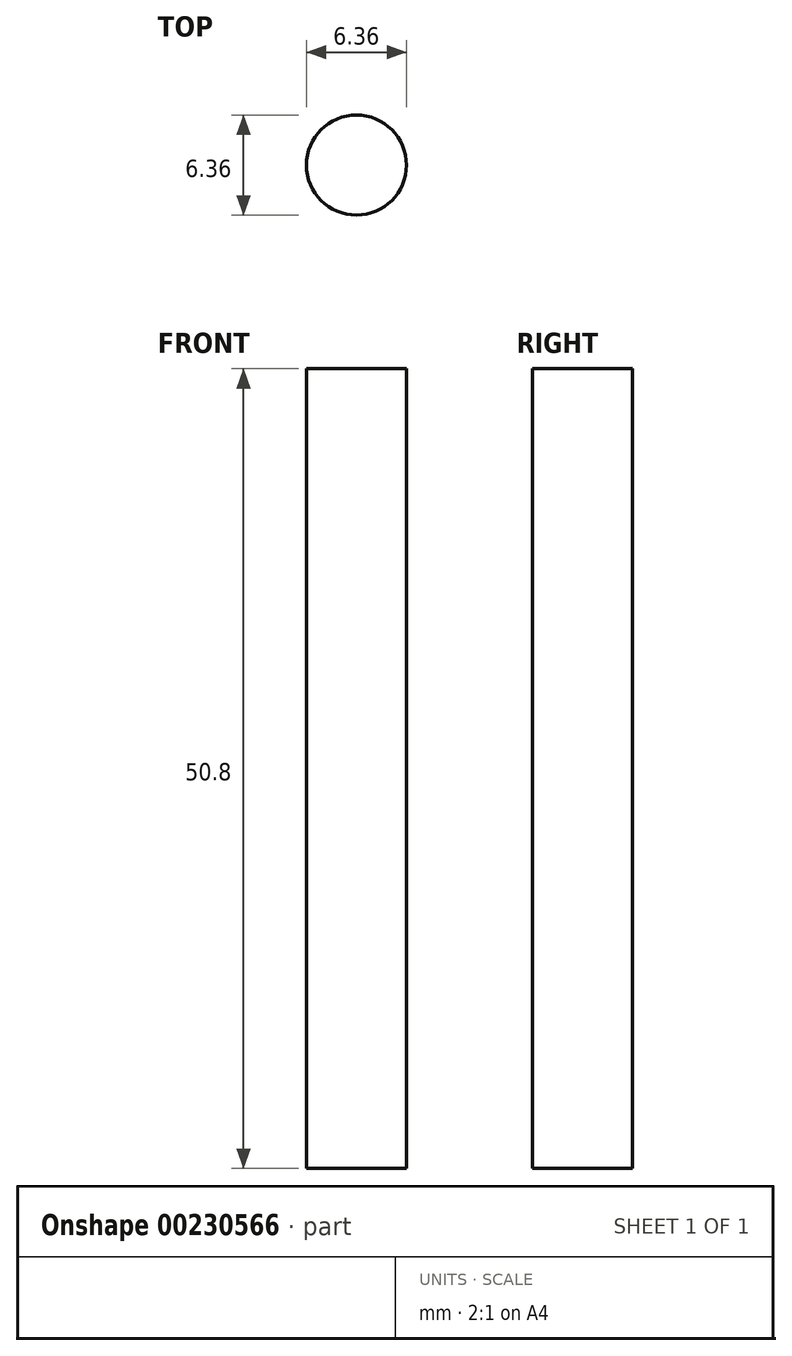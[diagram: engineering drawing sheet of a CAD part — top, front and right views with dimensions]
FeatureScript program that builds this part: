
annotation { "Feature Type Name" : "Feature", "Feature Type Description" : "" }
export const myFeature = defineFeature(function(context is Context, id is Id, definition is map)
    precondition{}
    {
        {
            var Q0;
            Q0=qCreatedBy(makeId("Top.planeOp"),FACE);
            var sketch = newSketch(context, id + "F0", { "sketchPlane" : qUnion([Q0])});
            skCircle(sketch, "E0", {"center": v(0, 0) * mm, "radius": 3.18 * mm});
            skSolve(sketch);
        }
        {
            var Q0;
            Q0=sQuery(id+"F0.wireOp",EDGE,"E0");
            extrude(context, id + "F1", {"bodyType" : ToolBodyType.SURFACE, "surfaceEntities" : qUnion([Q0]), "depth" : 50.8 * mm});
        }
    });
